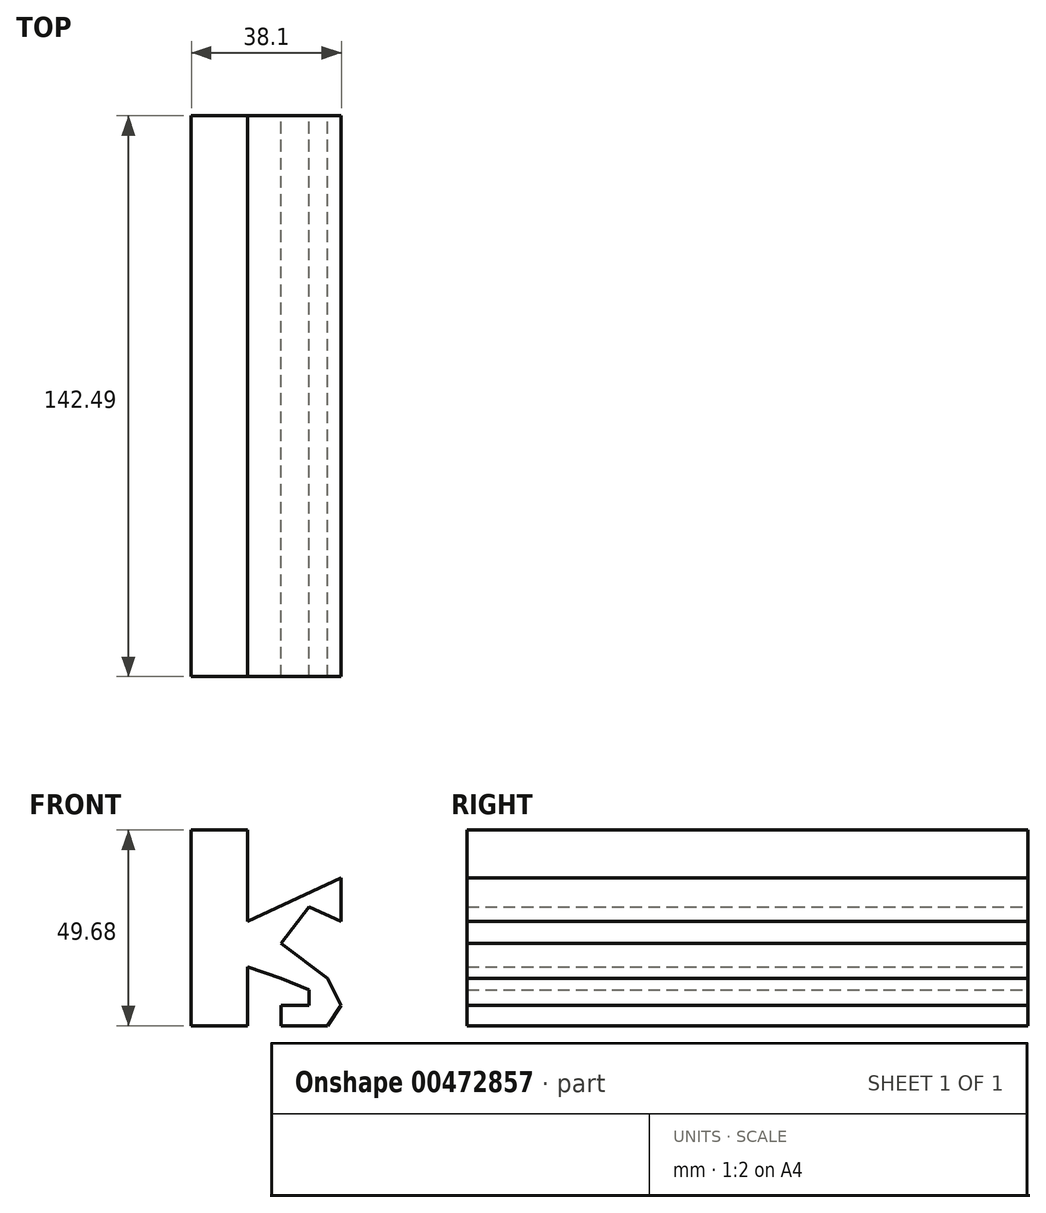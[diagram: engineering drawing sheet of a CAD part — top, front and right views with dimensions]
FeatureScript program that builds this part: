
annotation { "Feature Type Name" : "Feature", "Feature Type Description" : "" }
export const myFeature = defineFeature(function(context is Context, id is Id, definition is map)
    precondition{}
    {
        {
            var Q0;
            Q0=qCreatedBy(makeId("Front.planeOp"),FACE);
            var sketch = newSketch(context, id + "F0", { "sketchPlane" : qUnion([Q0])});
            skLineSegment(sketch, "E0", {"start": v(-47.24, 28.8) * mm, "end": v(-47.24, -20.88) * mm});
            skLineSegment(sketch, "E1", {"start": v(-47.24, -20.88) * mm, "end": v(-32.92, -20.88) * mm});
            skLineSegment(sketch, "E2", {"start": v(-32.92, -20.88) * mm, "end": v(-32.92, -5.94) * mm});
            skLineSegment(sketch, "E3", {"start": v(-47.24, 28.8) * mm, "end": v(-32.92, 28.8) * mm});
            skLineSegment(sketch, "E4", {"start": v(-32.92, 28.8) * mm, "end": v(-32.92, 9.9) * mm});
            skLineSegment(sketch, "E5", {"start": v(-9.14, 16.61) * mm, "end": v(-9.14, 5.64) * mm});
            skLineSegment(sketch, "E6", {"start": v(-9.14, 5.64) * mm, "end": v(-17.37, 9.3) * mm});
            skLineSegment(sketch, "E7", {"start": v(-17.37, 9.3) * mm, "end": v(-24.38, 0) * mm});
            skLineSegment(sketch, "E8", {"start": v(-24.38, 0) * mm, "end": v(-12.63, -8.86) * mm});
            skLineSegment(sketch, "E9", {"start": v(-12.63, -8.86) * mm, "end": v(-9.14, -15.7) * mm});
            skLineSegment(sketch, "E10", {"start": v(-9.14, -15.7) * mm, "end": v(-12.63, -20.88) * mm});
            skLineSegment(sketch, "E11", {"start": v(-12.63, -20.88) * mm, "end": v(-24.38, -20.88) * mm});
            skLineSegment(sketch, "E12", {"start": v(-24.38, -20.88) * mm, "end": v(-24.38, -15.7) * mm});
            skLineSegment(sketch, "E13", {"start": v(-24.38, -15.7) * mm, "end": v(-20.73, -15.7) * mm});
            skLineSegment(sketch, "E14", {"start": v(-20.73, -15.7) * mm, "end": v(-17.37, -15.7) * mm});
            skLineSegment(sketch, "E15", {"start": v(-17.37, -15.7) * mm, "end": v(-17.37, -11.73) * mm});
            skLineSegment(sketch, "E16", {"start": v(-17.37, -11.73) * mm, "end": v(-24.38, -8.86) * mm});
            skLineSegment(sketch, "E17", {"start": v(-24.38, -8.86) * mm, "end": v(-32.92, -5.94) * mm});
            skLineSegment(sketch, "E18", {"start": v(-32.92, 5.64) * mm, "end": v(-32.92, 9.9) * mm});
            skLineSegment(sketch, "E19", {"start": v(-9.14, 16.61) * mm, "end": v(-32.92, 5.64) * mm});
            skSolve(sketch);
        }
        {
            var Q0;
            Q0 = qSketchRegion(id + "F0", true);
            extrude(context, id + "F1", {"entities" : qUnion([Q0]), "depth" : 142.5 * mm});
        }
    });
